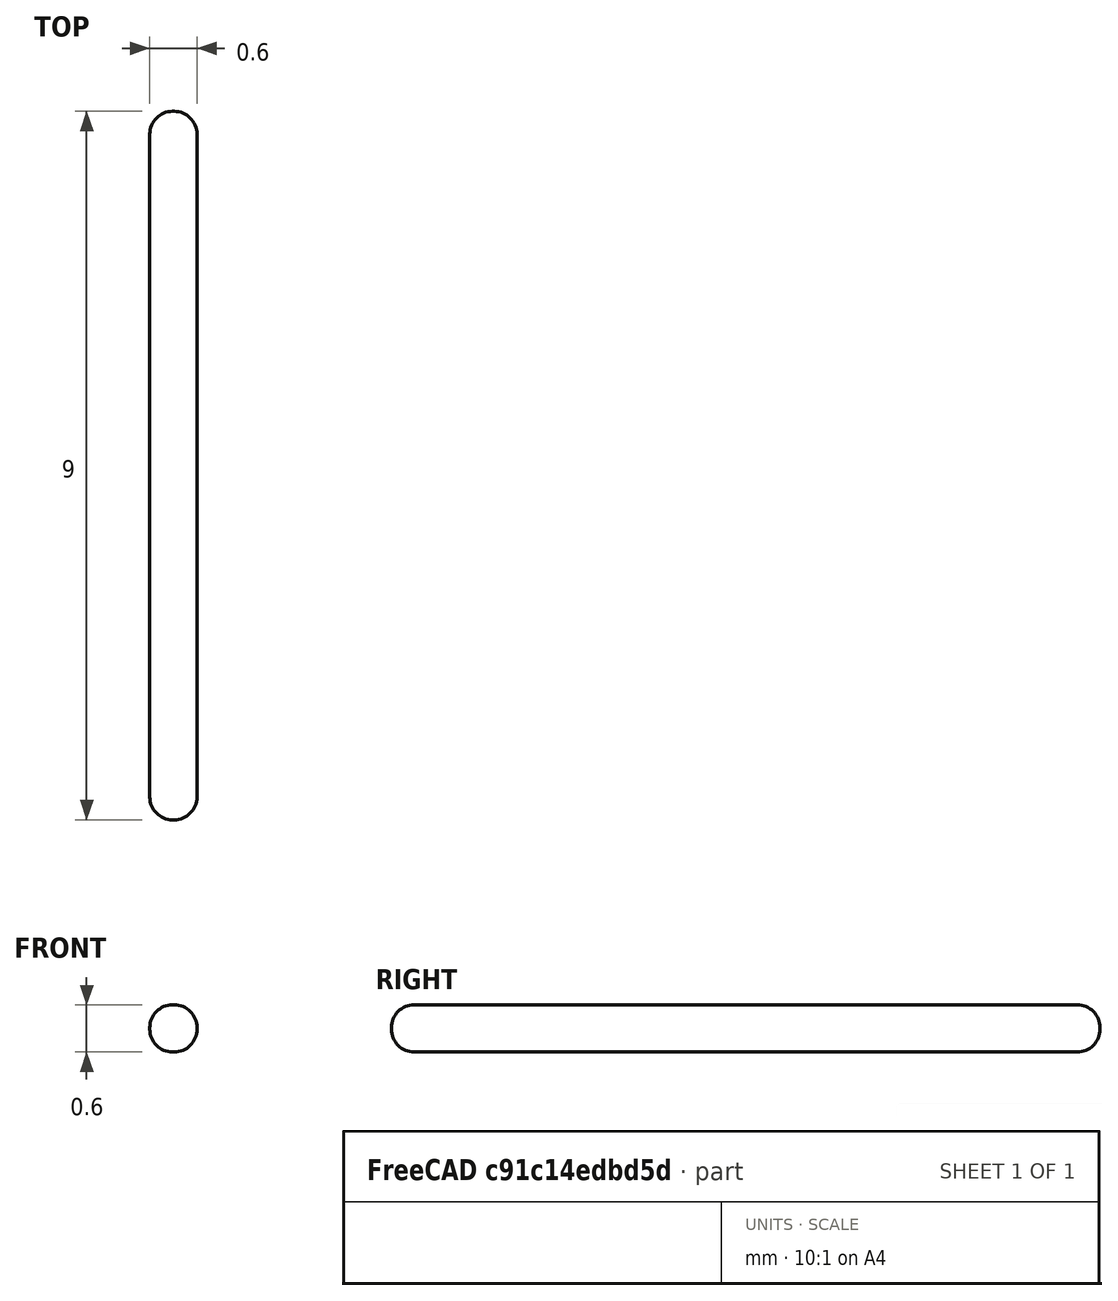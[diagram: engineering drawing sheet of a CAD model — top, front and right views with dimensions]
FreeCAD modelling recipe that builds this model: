
FCSTD DOCUMENT  (FreeCAD 0.16R6712 (Git))
Label: 1s
License: All rights reserved
LicenseURL: http://en.wikipedia.org/wiki/All_rights_reserved
objects: Sketcher::SketchObject×1, PartDesign::Pad×1, PartDesign::Fillet×1, Mesh::Feature×1
note: 4 computed .brp shape members not serialized (recipe doc carries the construction recipe); baked Part::Feature solids carry a one-line shape summary decoded from their .brp

FEATURE [Sketcher::SketchObject] Sketch
  sketch-geometry (4):
    g0: LineSegment StartX=-0.3 StartY=0 StartZ=0 EndX=0.3 EndY=0 EndZ=0
    g1: LineSegment StartX=0.3 StartY=0 StartZ=0 EndX=0.3 EndY=9 EndZ=0
    g2: LineSegment StartX=0.3 StartY=9 StartZ=0 EndX=-0.3 EndY=9 EndZ=0
    g3: LineSegment StartX=-0.3 StartY=9 StartZ=0 EndX=-0.3 EndY=0 EndZ=0
  constraints (12):
    c: Coincident(g0,g1)
    c: Coincident(g1,g2)
    c: Coincident(g2,g3)
    c: Coincident(g3,g0)
    c: Horizontal(g0)
    c: Horizontal(g2)
    c: Vertical(g1)
    c: Vertical(g3)
    c: PointOnObject(g-1,g0)
    c: Distance(g1,g0) = 9
    c: Distance(g2,g1) = 0.6
    c: DistanceX(g-2,g0) = 0.3
FEATURE [PartDesign::Pad] Pad
  Length = 0.6
  Length2 = 100
  Midplane = true
  Sketch = -> Sketch
  Type = 0
FEATURE [PartDesign::Fillet] Fillet
  Base = -> Pad [Edge4,Edge7,Edge10,Edge12,Edge8,Edge1,Edge11,Edge3,Edge6,Edge9,Edge2,Edge5]
  Radius = 0.29
FEATURE [Mesh::Feature] Mesh  label="Fillet (Meshed)"
